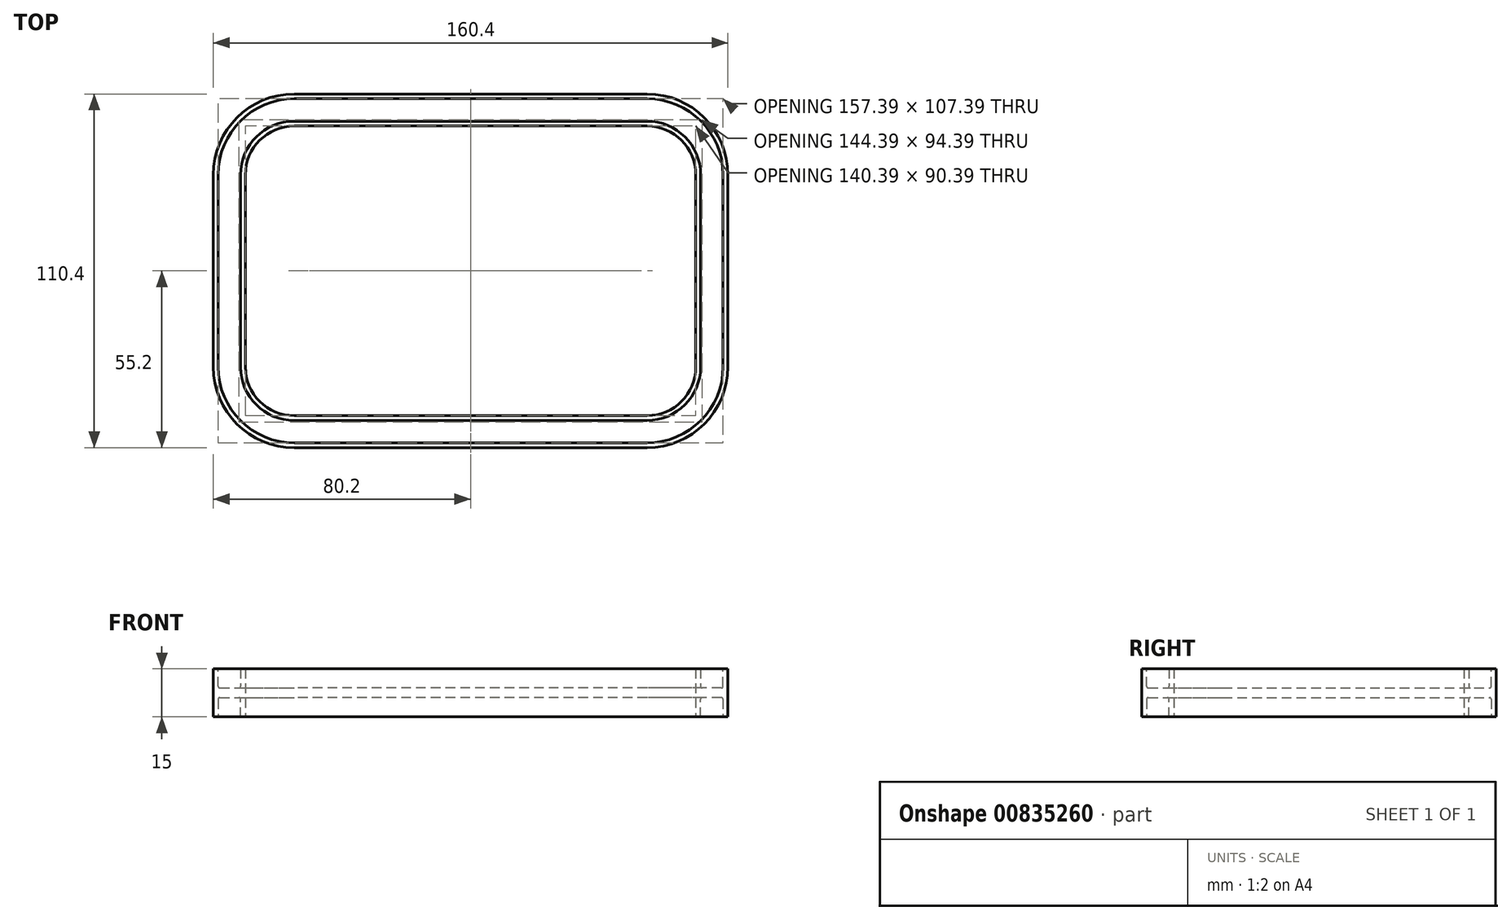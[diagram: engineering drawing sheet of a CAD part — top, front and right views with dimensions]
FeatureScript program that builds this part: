
annotation { "Feature Type Name" : "Feature", "Feature Type Description" : "" }
export const myFeature = defineFeature(function(context is Context, id is Id, definition is map)
    precondition{}
    {
        {
            var Q0;
            Q0=qCreatedBy(makeId("Top.planeOp"),FACE);
            var sketch = newSketch(context, id + "F0", { "sketchPlane" : qUnion([Q0])});
            skLineSegment(sketch, "E0.bottom", {"start": v(55, 50) * mm, "end": v(-55, 50) * mm});
            skLineSegment(sketch, "E0.top", {"start": v(55, -50) * mm, "end": v(-55, -50) * mm});
            skLineSegment(sketch, "E0.left", {"start": v(75, 30) * mm, "end": v(75, -30) * mm});
            skLineSegment(sketch, "E0.right", {"start": v(-75, 30) * mm, "end": v(-75, -30) * mm});
            skPoint(sketch, "E0.middle", {"position": v(0, 0) * mm});
            skPoint(sketch, "E1.visualSharp", {"position": v(-75, 50) * mm});
            skArc(sketch, "E1.filletArc", {"start": v(-55, 50) * mm, "mid": v(-69.14, 44.14) * mm, "end": v(-75, 30) * mm});
            skPoint(sketch, "E2.visualSharp", {"position": v(75, 50) * mm});
            skArc(sketch, "E2.filletArc", {"start": v(75, 30) * mm, "mid": v(69.14, 44.14) * mm, "end": v(55, 50) * mm});
            skPoint(sketch, "E3.visualSharp", {"position": v(75, -50) * mm});
            skArc(sketch, "E3.filletArc", {"start": v(55, -50) * mm, "mid": v(69.14, -44.14) * mm, "end": v(75, -30) * mm});
            skPoint(sketch, "E4.visualSharp", {"position": v(-75, -50) * mm});
            skArc(sketch, "E4.filletArc", {"start": v(-75, -30) * mm, "mid": v(-69.14, -44.14) * mm, "end": v(-55, -50) * mm});
            skSolve(sketch);
        }
        {
            var Q0;
            Q0=qCreatedBy(makeId("Right.planeOp"),FACE);
            var sketch = newSketch(context, id + "F1", { "sketchPlane" : qUnion([Q0])});
            skLineSegment(sketch, "E5.bottom", {"start": v(55.2, 7.5) * mm, "end": v(45.2, 7.5) * mm});
            skLineSegment(sketch, "E5.top", {"start": v(55.2, -7.5) * mm, "end": v(45.2, -7.5) * mm});
            skLineSegment(sketch, "E5.left", {"start": v(55.2, 7.5) * mm, "end": v(55.2, -7.5) * mm});
            skLineSegment(sketch, "E5.right", {"start": v(45.2, 7.5) * mm, "end": v(45.2, -7.5) * mm});
            skPoint(sketch, "E5.middle", {"position": v(50.2, 0) * mm});
            skLineSegment(sketch, "E6", {"start": v(50.2, 0) * mm, "end": v(55.2, 0) * mm});
            skLineSegment(sketch, "E7", {"start": v(55.2, 7.5) * mm, "end": v(53.7, 7.5) * mm});
            skLineSegment(sketch, "E8", {"start": v(45.2, 7.5) * mm, "end": v(46.7, 7.5) * mm});
            skLineSegment(sketch, "E9", {"start": v(46.7, 7.5) * mm, "end": v(46.7, 2) * mm});
            skLineSegment(sketch, "E10", {"start": v(47.2, 1.5) * mm, "end": v(53.2, 1.5) * mm});
            skLineSegment(sketch, "E11", {"start": v(53.7, 2) * mm, "end": v(53.7, 7.5) * mm});
            skLineSegment(sketch, "E12.MirrorCS", {"start": v(47.2, -1.5) * mm, "end": v(53.2, -1.5) * mm});
            skLineSegment(sketch, "E13.MirrorCS", {"start": v(53.7, -2) * mm, "end": v(53.7, -7.5) * mm});
            skLineSegment(sketch, "E14.MirrorCS", {"start": v(46.7, -7.5) * mm, "end": v(46.7, -2) * mm});
            skPoint(sketch, "E15.visualSharp", {"position": v(46.7, 1.5) * mm});
            skArc(sketch, "E15.filletArc", {"start": v(46.7, 2) * mm, "mid": v(46.84, 1.65) * mm, "end": v(47.2, 1.5) * mm});
            skPoint(sketch, "E16.visualSharp", {"position": v(53.7, 1.5) * mm});
            skArc(sketch, "E16.filletArc", {"start": v(53.2, 1.5) * mm, "mid": v(53.55, 1.65) * mm, "end": v(53.7, 2) * mm});
            skPoint(sketch, "E17.visualSharp", {"position": v(53.7, -1.5) * mm});
            skArc(sketch, "E17.filletArc", {"start": v(53.7, -2) * mm, "mid": v(53.55, -1.65) * mm, "end": v(53.2, -1.5) * mm});
            skPoint(sketch, "E18.visualSharp", {"position": v(46.7, -1.5) * mm});
            skArc(sketch, "E18.filletArc", {"start": v(47.2, -1.5) * mm, "mid": v(46.84, -1.65) * mm, "end": v(46.7, -2) * mm});
            skSolve(sketch);
        }
        {
            var Q0;
            {var subQ1=sQuery(id+"F1.wireOp",EDGE,"E5.right");Q0=makeQuery(id+"F1.imprint","IMPRINT",FACE,{"disambiguationData":[TD([[makeQuery(id+"F1.imprint","IMPRINT",EDGE,{"derivedFrom":subQ1}),1.0]])]});}
            var Q1;
            Q1=sQuery(id+"F0.wireOp",EDGE,"E0.bottom");
            var Q2;
            Q2=sQuery(id+"F0.wireOp",EDGE,"E2.filletArc");
            var Q3;
            Q3=sQuery(id+"F0.wireOp",EDGE,"E0.left");
            var Q4;
            Q4=sQuery(id+"F0.wireOp",EDGE,"E3.filletArc");
            var Q5;
            Q5=sQuery(id+"F0.wireOp",EDGE,"E0.top");
            var Q6;
            Q6=sQuery(id+"F0.wireOp",EDGE,"E4.filletArc");
            var Q7;
            Q7=sQuery(id+"F0.wireOp",EDGE,"E0.right");
            var Q8;
            Q8=sQuery(id+"F0.wireOp",EDGE,"E1.filletArc");
            sweep(context, id + "F2", {"profiles" : qUnion([Q0]), "path" : qUnion([Q1, Q2, Q3, Q4, Q5, Q6, Q7, Q8])});
        }
    });
